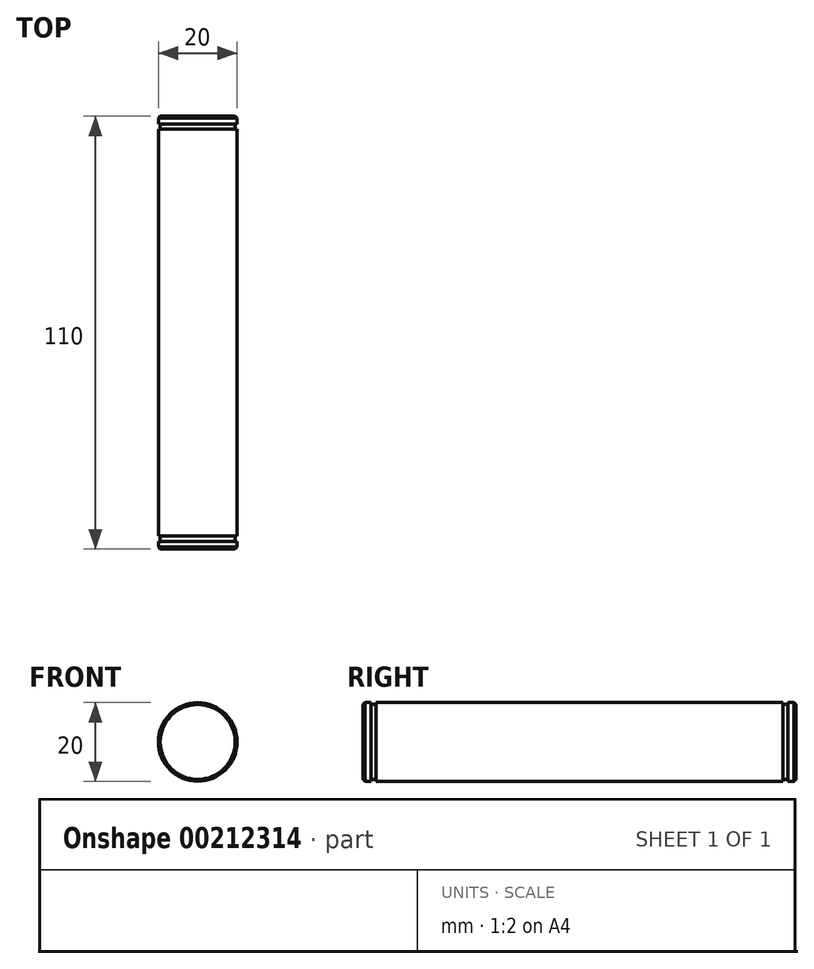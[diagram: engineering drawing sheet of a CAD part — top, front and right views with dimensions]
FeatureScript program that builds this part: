
annotation { "Feature Type Name" : "Feature", "Feature Type Description" : "" }
export const myFeature = defineFeature(function(context is Context, id is Id, definition is map)
    precondition{}
    {
        {
            var Q0;
            Q0=qCreatedBy(makeId("Front.planeOp"),FACE);
            var sketch = newSketch(context, id + "F0", { "sketchPlane" : qUnion([Q0])});
            skCircle(sketch, "E0", {"center": v(0, 0) * mm, "radius": 10 * mm});
            skSolve(sketch);
        }
        {
            var Q0;
            Q0 = qSketchRegion(id + "F0", true);
            extrude(context, id + "F1", {"entities" : qUnion([Q0]), "depth" : 110 * mm});
        }
        {
            var Q0;
            Q0=makeQuery(id+"F1.opExtrude","CAP_FACE",FACE,{"disambiguationData":[OSD([sQuery(id+"F0.wireOp",EDGE,"E0")])],"isStart":false});
            cPlane(context, id + "F2", {"entities" : qUnion([Q0]), "cplaneType" : CPlaneType.OFFSET, "offset" : 2 * mm, "oppositeDirection" : true, "width" : 150 * mm, "height" : 150 * mm});
        }
        {
            var Q0;
            Q0=qCreatedBy(id+"F2.planeOp",FACE);
            var sketch = newSketch(context, id + "F3", { "sketchPlane" : qUnion([Q0])});
            skCircle(sketch, "E1", {"center": v(0, 0) * mm, "radius": 9.5 * mm});
            skCircle(sketch, "E2", {"center": v(0, 0) * mm, "radius": 10 * mm});
            skSolve(sketch);
        }
        {
            var Q0;
            Q0 = qSketchRegion(id + "F3", true);
            extrude(context, id + "F4", {"entities" : qUnion([Q0]), "operationType" : NewBodyOperationType.REMOVE, "oppositeDirection" : true, "depth" : 1.3 * mm});
        }
        {
            var Q0;
            Q0=makeQuery(id+"F1.opExtrude","CAP_FACE",FACE,{"disambiguationData":[OSD([sQuery(id+"F0.wireOp",EDGE,"E0")])],"isStart":true});
            cPlane(context, id + "F5", {"entities" : qUnion([Q0]), "cplaneType" : CPlaneType.OFFSET, "offset" : 2 * mm, "oppositeDirection" : true, "width" : 150 * mm, "height" : 150 * mm});
        }
        {
            var Q0;
            Q0=qCreatedBy(id+"F5.planeOp",FACE);
            var sketch = newSketch(context, id + "F6", { "sketchPlane" : qUnion([Q0])});
            skCircle(sketch, "E3", {"center": v(0, 0) * mm, "radius": 9.5 * mm});
            skCircle(sketch, "E4", {"center": v(0, 0) * mm, "radius": 10 * mm});
            skSolve(sketch);
        }
        {
            var Q0;
            Q0 = qSketchRegion(id + "F6", true);
            extrude(context, id + "F7", {"entities" : qUnion([Q0]), "operationType" : NewBodyOperationType.REMOVE, "oppositeDirection" : true, "depth" : 1.3 * mm});
        }
        {
            var Q0;
            Q0=makeQuery(id+"F1.opExtrude","CAP_EDGE",EDGE,{"disambiguationData":[OSD([sQuery(id+"F0.wireOp",EDGE,"E0")])],"isStart":false});
            var Q1;
            Q1=makeQuery(id+"F1.opExtrude","CAP_EDGE",EDGE,{"disambiguationData":[OSD([sQuery(id+"F0.wireOp",EDGE,"E0")])],"isStart":true});
            chamfer(context, id + "F8", {"entities" : qUnion([Q0, Q1]), "width" : .5 * mm, "tangentPropagation" : true});
        }
    });
